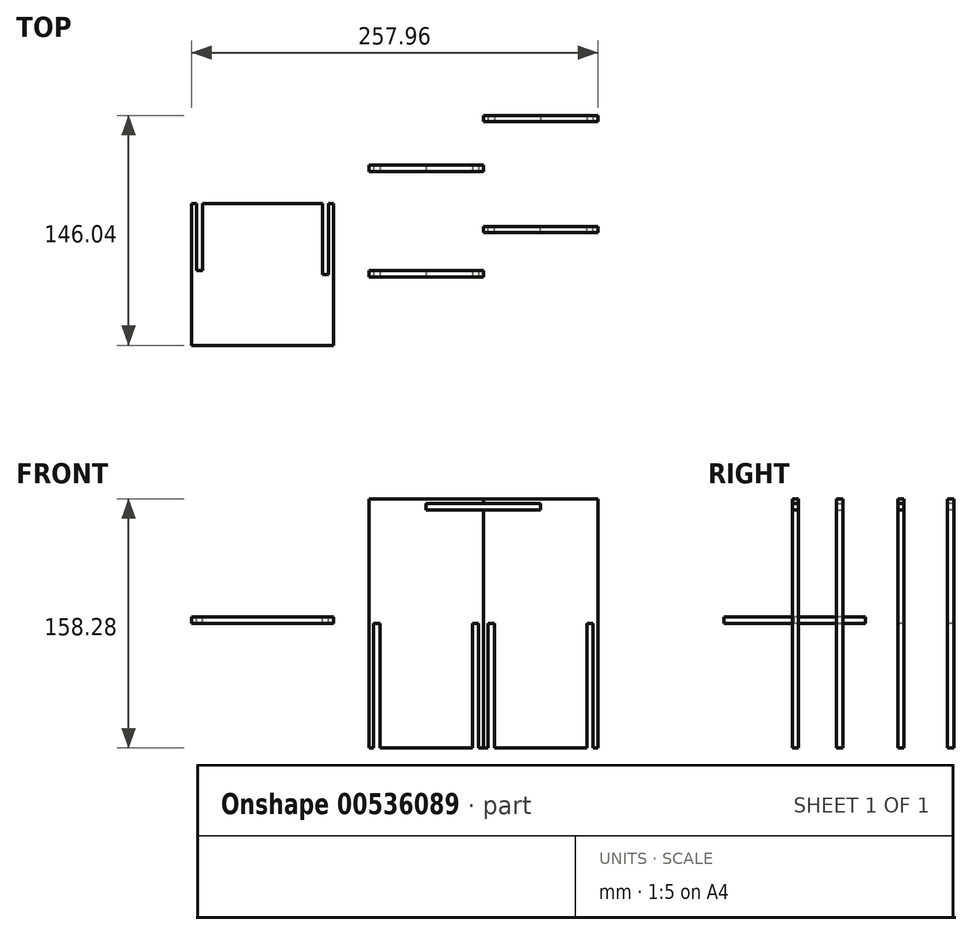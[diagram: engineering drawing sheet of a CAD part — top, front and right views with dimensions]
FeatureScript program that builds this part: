
annotation { "Feature Type Name" : "Feature", "Feature Type Description" : "" }
export const myFeature = defineFeature(function(context is Context, id is Id, definition is map)
    precondition{}
    {
        {
            var Q0;
            Q0=qCreatedBy(makeId("Front.planeOp"),FACE);
            var sketch = newSketch(context, id + "F0", { "sketchPlane" : qUnion([Q0])});
            skLineSegment(sketch, "E0.bottom", {"start": v(36.36, -79.14) * mm, "end": v(-36.36, -79.14) * mm});
            skLineSegment(sketch, "E0.top", {"start": v(36.36, 79.14) * mm, "end": v(-36.36, 79.14) * mm});
            skLineSegment(sketch, "E0.left", {"start": v(36.36, -79.14) * mm, "end": v(36.36, 79.14) * mm});
            skLineSegment(sketch, "E0.right", {"start": v(-36.36, -79.14) * mm, "end": v(-36.36, 79.14) * mm});
            skPoint(sketch, "E0.middle", {"position": v(0, 0) * mm});
            skSolve(sketch);
        }
        {
            var Q0;
            Q0 = qSketchRegion(id + "F0", true);
            extrude(context, id + "F1", {"entities" : qUnion([Q0]), "depth" : 4 * mm, "offsetDistance" : 25 * mm});
        }
        {
            var Q0;
            Q0=makeQuery(id+"F1.opExtrude","CAP_FACE",FACE,{"disambiguationData":[OSD([sQuery(id+"F0.wireOp",EDGE,"E0.bottom"),sQuery(id+"F0.wireOp",EDGE,"E0.top"),sQuery(id+"F0.wireOp",EDGE,"E0.left"),sQuery(id+"F0.wireOp",EDGE,"E0.right")])],"isStart":false});
            var sketch = newSketch(context, id + "F2", { "sketchPlane" : qUnion([Q0])});
            skLineSegment(sketch, "E1.bottom", {"start": v(-33.36, -79.14) * mm, "end": v(-29.36, -79.14) * mm});
            skLineSegment(sketch, "E1.top", {"start": v(-33.36, 0) * mm, "end": v(-29.36, 0) * mm});
            skLineSegment(sketch, "E1.left", {"start": v(-33.36, -79.14) * mm, "end": v(-33.36, 0) * mm});
            skLineSegment(sketch, "E1.right", {"start": v(-29.36, -79.14) * mm, "end": v(-29.36, 0) * mm});
            skSolve(sketch);
        }
        {
            var Q0;
            Q0 = qSketchRegion(id + "F2", true);
            extrude(context, id + "F3", {"entities" : qUnion([Q0]), "operationType" : NewBodyOperationType.REMOVE, "oppositeDirection" : true, "depth" : 25 * mm, "offsetDistance" : 25 * mm});
        }
        {
            var Q0;
            Q0=makeQuery(id+"F1.opExtrude","CAP_FACE",FACE,{"disambiguationData":[OSD([sQuery(id+"F0.wireOp",EDGE,"E0.bottom"),sQuery(id+"F0.wireOp",EDGE,"E0.top"),sQuery(id+"F0.wireOp",EDGE,"E0.left"),sQuery(id+"F0.wireOp",EDGE,"E0.right")])],"isStart":false});
            var sketch = newSketch(context, id + "F4", { "sketchPlane" : qUnion([Q0])});
            skLineSegment(sketch, "E2.bottom", {"start": v(29.36, -79.14) * mm, "end": v(33.36, -79.14) * mm});
            skLineSegment(sketch, "E2.top", {"start": v(29.36, 0) * mm, "end": v(33.36, 0) * mm});
            skLineSegment(sketch, "E2.left", {"start": v(29.36, -79.14) * mm, "end": v(29.36, 0) * mm});
            skLineSegment(sketch, "E2.right", {"start": v(33.36, -79.14) * mm, "end": v(33.36, 0) * mm});
            skSolve(sketch);
        }
        {
            var Q0;
            Q0 = qSketchRegion(id + "F4", true);
            extrude(context, id + "F5", {"entities" : qUnion([Q0]), "operationType" : NewBodyOperationType.REMOVE, "oppositeDirection" : true, "depth" : 25 * mm, "offsetDistance" : 25 * mm});
        }
        {
            var Q0;
            Q0=makeQuery(id+"F1.opExtrude","CAP_FACE",FACE,{"disambiguationData":[OSD([sQuery(id+"F0.wireOp",EDGE,"E0.bottom"),sQuery(id+"F0.wireOp",EDGE,"E0.top"),sQuery(id+"F0.wireOp",EDGE,"E0.left"),sQuery(id+"F0.wireOp",EDGE,"E0.right")])],"isStart":false});
            var sketch = newSketch(context, id + "F6", { "sketchPlane" : qUnion([Q0])});
            skLineSegment(sketch, "E3.bottom", {"start": v(36.36, 76.14) * mm, "end": v(0, 76.14) * mm});
            skLineSegment(sketch, "E3.top", {"start": v(36.36, 72.14) * mm, "end": v(0, 72.14) * mm});
            skLineSegment(sketch, "E3.left", {"start": v(36.36, 76.14) * mm, "end": v(36.36, 72.14) * mm});
            skLineSegment(sketch, "E3.right", {"start": v(0, 76.14) * mm, "end": v(0, 72.14) * mm});
            skSolve(sketch);
        }
        {
            var Q0;
            Q0 = qSketchRegion(id + "F6", true);
            extrude(context, id + "F7", {"entities" : qUnion([Q0]), "operationType" : NewBodyOperationType.REMOVE, "oppositeDirection" : true, "depth" : 25 * mm, "offsetDistance" : 25 * mm});
        }
        {
            var Q0;
            Q0=makeQuery(id+"F1.opExtrude","CAP_FACE",FACE,{"disambiguationData":[OSD([sQuery(id+"F0.wireOp",EDGE,"E0.bottom"),sQuery(id+"F0.wireOp",EDGE,"E0.top"),sQuery(id+"F0.wireOp",EDGE,"E0.left"),sQuery(id+"F0.wireOp",EDGE,"E0.right")])],"isStart":false});
            var sketch = newSketch(context, id + "F8", { "sketchPlane" : qUnion([Q0])});
            skSolve(sketch);
        }
        {
            var Q0;
            Q0 = qSketchRegion(id + "F8", true);
            var Q1;
            {var subQ4=sQuery(id+"F0.wireOp",EDGE,"E0.top");Q1=makeQuery(id+"F8.imprint","IMPRINT",FACE,{"disambiguationData":[TD([[makeQuery(id+"F8.imprint","IMPRINT",EDGE,{"derivedFrom":makeQuery(id+"F1.opExtrude","CAP_EDGE",EDGE,{"disambiguationData":[OSD([subQ4])],"isStart":false})}),1.0]])]});}
            extrude(context, id + "F9", {"entities" : qUnion([Q0, Q1]), "depth" : 4 * mm, "offsetDistance" : 25 * mm});
        }
        {
            var Q0;
            Q0=makeQuery(id+"F9.opExtrude","SWEPT_BODY",BODY,{"disambiguationData":[OSD([sQuery(id+"F0.wireOp",EDGE,"E0.bottom"),sQuery(id+"F0.wireOp",EDGE,"E0.top"),sQuery(id+"F0.wireOp",EDGE,"E0.left"),sQuery(id+"F0.wireOp",EDGE,"E0.right"),sQuery(id+"F2.wireOp",EDGE,"E1.top"),sQuery(id+"F2.wireOp",EDGE,"E1.left"),sQuery(id+"F2.wireOp",EDGE,"E1.right"),sQuery(id+"F4.wireOp",EDGE,"E2.top"),sQuery(id+"F4.wireOp",EDGE,"E2.left"),sQuery(id+"F4.wireOp",EDGE,"E2.right"),sQuery(id+"F6.wireOp",EDGE,"E3.bottom"),sQuery(id+"F6.wireOp",EDGE,"E3.top"),sQuery(id+"F6.wireOp",EDGE,"E3.right")])]});
            transform(context, id + "F10", {"entities" : qUnion([Q0]), "transformType" : TransformType.TRANSLATION_3D, "dx" : 0 * mm, "dy" : 98.5 * mm, "dz" : 0 * mm, "makeCopy" : false});
        }
        {
            var Q0;
            Q0=makeQuery(id+"F1.opExtrude","CAP_FACE",FACE,{"disambiguationData":[OSD([sQuery(id+"F0.wireOp",EDGE,"E0.bottom"),sQuery(id+"F0.wireOp",EDGE,"E0.top"),sQuery(id+"F0.wireOp",EDGE,"E0.left"),sQuery(id+"F0.wireOp",EDGE,"E0.right")])],"isStart":true});
            var sketch = newSketch(context, id + "F11", { "sketchPlane" : qUnion([Q0])});
            skSolve(sketch);
        }
        {
            var Q0;
            Q0 = qSketchRegion(id + "F11", true);
            var Q1;
            {var subQ4=sQuery(id+"F0.wireOp",EDGE,"E0.top");Q1=makeQuery(id+"F11.imprint","IMPRINT",FACE,{"disambiguationData":[TD([[makeQuery(id+"F11.imprint","IMPRINT",EDGE,{"derivedFrom":makeQuery(id+"F1.opExtrude","CAP_EDGE",EDGE,{"disambiguationData":[OSD([subQ4])],"isStart":true})}),-1.0]])]});}
            extrude(context, id + "F12", {"entities" : qUnion([Q0, Q1]), "depth" : 4 * mm, "offsetDistance" : 25 * mm});
        }
        {
            var Q0;
            Q0=makeQuery(id+"F12.opExtrude","SWEPT_BODY",BODY,{"disambiguationData":[OSD([sQuery(id+"F0.wireOp",EDGE,"E0.bottom"),sQuery(id+"F0.wireOp",EDGE,"E0.top"),sQuery(id+"F0.wireOp",EDGE,"E0.left"),sQuery(id+"F0.wireOp",EDGE,"E0.right"),sQuery(id+"F2.wireOp",EDGE,"E1.top"),sQuery(id+"F2.wireOp",EDGE,"E1.left"),sQuery(id+"F2.wireOp",EDGE,"E1.right"),sQuery(id+"F4.wireOp",EDGE,"E2.top"),sQuery(id+"F4.wireOp",EDGE,"E2.left"),sQuery(id+"F4.wireOp",EDGE,"E2.right"),sQuery(id+"F6.wireOp",EDGE,"E3.bottom"),sQuery(id+"F6.wireOp",EDGE,"E3.top"),sQuery(id+"F6.wireOp",EDGE,"E3.right")])]});
            transform(context, id + "F13", {"entities" : qUnion([Q0]), "transformType" : TransformType.TRANSLATION_3D, "dx" : 0 * mm, "dy" : 63 * mm, "dz" : 0 * mm, "makeCopy" : false});
        }
        {
            var Q0;
            Q0=makeQuery(id+"F1.opExtrude","CAP_FACE",FACE,{"disambiguationData":[OSD([sQuery(id+"F0.wireOp",EDGE,"E0.bottom"),sQuery(id+"F0.wireOp",EDGE,"E0.top"),sQuery(id+"F0.wireOp",EDGE,"E0.left"),sQuery(id+"F0.wireOp",EDGE,"E0.right")])],"isStart":true});
            var sketch = newSketch(context, id + "F14", { "sketchPlane" : qUnion([Q0])});
            skSolve(sketch);
        }
        {
            var Q0;
            Q0 = qSketchRegion(id + "F14", true);
            var Q1;
            {var subQ4=sQuery(id+"F0.wireOp",EDGE,"E0.top");Q1=makeQuery(id+"F14.imprint","IMPRINT",FACE,{"disambiguationData":[TD([[makeQuery(id+"F14.imprint","IMPRINT",EDGE,{"derivedFrom":makeQuery(id+"F1.opExtrude","CAP_EDGE",EDGE,{"disambiguationData":[OSD([subQ4])],"isStart":true})}),-1.0]])]});}
            extrude(context, id + "F15", {"entities" : qUnion([Q0, Q1]), "depth" : 4 * mm, "offsetDistance" : 25 * mm});
        }
        {
            var Q0;
            Q0=makeQuery(id+"F15.opExtrude","SWEPT_BODY",BODY,{"disambiguationData":[OSD([sQuery(id+"F0.wireOp",EDGE,"E0.bottom"),sQuery(id+"F0.wireOp",EDGE,"E0.top"),sQuery(id+"F0.wireOp",EDGE,"E0.left"),sQuery(id+"F0.wireOp",EDGE,"E0.right"),sQuery(id+"F2.wireOp",EDGE,"E1.top"),sQuery(id+"F2.wireOp",EDGE,"E1.left"),sQuery(id+"F2.wireOp",EDGE,"E1.right"),sQuery(id+"F4.wireOp",EDGE,"E2.top"),sQuery(id+"F4.wireOp",EDGE,"E2.left"),sQuery(id+"F4.wireOp",EDGE,"E2.right"),sQuery(id+"F6.wireOp",EDGE,"E3.bottom"),sQuery(id+"F6.wireOp",EDGE,"E3.top"),sQuery(id+"F6.wireOp",EDGE,"E3.right")])]});
            transform(context, id + "F16", {"entities" : qUnion([Q0]), "transformType" : TransformType.TRANSLATION_3D, "dx" : 0 * mm, "dy" : 28 * mm, "dz" : 0 * mm, "makeCopy" : false});
        }
        {
            var Q0;
            Q0=makeQuery(id+"F15.opExtrude","SWEPT_BODY",BODY,{"disambiguationData":[OSD([sQuery(id+"F0.wireOp",EDGE,"E0.bottom"),sQuery(id+"F0.wireOp",EDGE,"E0.top"),sQuery(id+"F0.wireOp",EDGE,"E0.left"),sQuery(id+"F0.wireOp",EDGE,"E0.right"),sQuery(id+"F2.wireOp",EDGE,"E1.top"),sQuery(id+"F2.wireOp",EDGE,"E1.left"),sQuery(id+"F2.wireOp",EDGE,"E1.right"),sQuery(id+"F4.wireOp",EDGE,"E2.top"),sQuery(id+"F4.wireOp",EDGE,"E2.left"),sQuery(id+"F4.wireOp",EDGE,"E2.right"),sQuery(id+"F6.wireOp",EDGE,"E3.bottom"),sQuery(id+"F6.wireOp",EDGE,"E3.top"),sQuery(id+"F6.wireOp",EDGE,"E3.right")])]});
            var Q1;
            {var subQ0=sQuery(id+"F0.wireOp",EDGE,"E0.bottom");var subQ1=sQuery(id+"F0.wireOp",EDGE,"E0.left");Q1=makeQuery(id+"F15.opExtrude","CAP_EDGE",EDGE,{"disambiguationData":[OSD([subQ1]),TDD([makeQuery(id+"F14.imprint","IMPRINT",EDGE,{"derivedFrom":makeQuery(id+"F7.boolean.opBoolean","SPLIT",EDGE,{"disambiguationData":[TD([makeQuery(id+"F1.opExtrude","SWEPT_FACE",FACE,{"disambiguationData":[OSD([subQ0])]})])],"derivedFrom":makeQuery(id+"F1.opExtrude","CAP_EDGE",EDGE,{"disambiguationData":[OSD([subQ1])],"isStart":true})})})])],"isStart":true});}
            transform(context, id + "F17", {"entities" : qUnion([Q0]), "transformType" : TransformType.ROTATION, "transformAxis" : qUnion([Q1]), "angle" : 180 * degree, "oppositeDirection" : true, "makeCopy" : false});
        }
        {
            var Q0;
            Q0=makeQuery(id+"F9.opExtrude","SWEPT_BODY",BODY,{"disambiguationData":[OSD([sQuery(id+"F0.wireOp",EDGE,"E0.bottom"),sQuery(id+"F0.wireOp",EDGE,"E0.top"),sQuery(id+"F0.wireOp",EDGE,"E0.left"),sQuery(id+"F0.wireOp",EDGE,"E0.right"),sQuery(id+"F2.wireOp",EDGE,"E1.top"),sQuery(id+"F2.wireOp",EDGE,"E1.left"),sQuery(id+"F2.wireOp",EDGE,"E1.right"),sQuery(id+"F4.wireOp",EDGE,"E2.top"),sQuery(id+"F4.wireOp",EDGE,"E2.left"),sQuery(id+"F4.wireOp",EDGE,"E2.right"),sQuery(id+"F6.wireOp",EDGE,"E3.bottom"),sQuery(id+"F6.wireOp",EDGE,"E3.top"),sQuery(id+"F6.wireOp",EDGE,"E3.right")])]});
            var Q1;
            {var subQ0=sQuery(id+"F0.wireOp",EDGE,"E0.bottom");var subQ1=sQuery(id+"F0.wireOp",EDGE,"E0.left");Q1=makeQuery(id+"F9.opExtrude","CAP_EDGE",EDGE,{"disambiguationData":[OSD([subQ1]),TDD([makeQuery(id+"F8.imprint","IMPRINT",EDGE,{"derivedFrom":makeQuery(id+"F7.boolean.opBoolean","SPLIT",EDGE,{"disambiguationData":[TD([makeQuery(id+"F1.opExtrude","SWEPT_FACE",FACE,{"disambiguationData":[OSD([subQ0])]})])],"derivedFrom":makeQuery(id+"F1.opExtrude","CAP_EDGE",EDGE,{"disambiguationData":[OSD([subQ1])],"isStart":false})})})])],"isStart":true});}
            transform(context, id + "F18", {"entities" : qUnion([Q0]), "transformType" : TransformType.ROTATION, "transformAxis" : qUnion([Q1]), "angle" : 180 * degree, "makeCopy" : false});
        }
        {
            var Q0;
            Q0=qCreatedBy(makeId("Top.planeOp"),FACE);
            var sketch = newSketch(context, id + "F19", { "sketchPlane" : qUnion([Q0])});
            skLineSegment(sketch, "E4.bottom", {"start": v(-148.88, 42.46) * mm, "end": v(-58.88, 42.46) * mm});
            skLineSegment(sketch, "E4.top", {"start": v(-148.88, -47.54) * mm, "end": v(-58.88, -47.54) * mm});
            skLineSegment(sketch, "E4.left", {"start": v(-148.88, 42.46) * mm, "end": v(-148.88, -47.54) * mm});
            skLineSegment(sketch, "E4.right", {"start": v(-58.88, 42.46) * mm, "end": v(-58.88, -47.54) * mm});
            skSolve(sketch);
        }
        {
            var Q0;
            Q0=makeQuery(id+"F19.imprint","IMPRINT",FACE,{"disambiguationData":[TD([[makeQuery(id+"F19.imprint","IMPRINT",EDGE,{"derivedFrom":sQuery(id+"F19.wireOp",EDGE,"E4.bottom")}),-1.0]])]});
            extrude(context, id + "F20", {"entities" : qUnion([Q0]), "depth" : 4 * mm, "offsetDistance" : 25 * mm});
        }
        {
            var Q0;
            Q0=makeQuery(id+"F20.opExtrude","CAP_FACE",FACE,{"disambiguationData":[OSD([sQuery(id+"F19.wireOp",EDGE,"E4.bottom"),sQuery(id+"F19.wireOp",EDGE,"E4.top"),sQuery(id+"F19.wireOp",EDGE,"E4.left"),sQuery(id+"F19.wireOp",EDGE,"E4.right")])],"isStart":false});
            var sketch = newSketch(context, id + "F21", { "sketchPlane" : qUnion([Q0])});
            skLineSegment(sketch, "E5", {"start": v(-148.88, -2.54) * mm, "end": v(-58.88, -2.54) * mm});
            skLineSegment(sketch, "E6.bottom", {"start": v(-65.88, 42.46) * mm, "end": v(-61.88, 42.46) * mm});
            skLineSegment(sketch, "E6.top", {"start": v(-65.88, -2.54) * mm, "end": v(-61.88, -2.54) * mm});
            skLineSegment(sketch, "E6.left", {"start": v(-65.88, 42.46) * mm, "end": v(-65.88, -2.54) * mm});
            skLineSegment(sketch, "E6.right", {"start": v(-61.88, 42.46) * mm, "end": v(-61.88, -2.54) * mm});
            skSolve(sketch);
        }
        {
            var Q0;
            Q0 = qSketchRegion(id + "F21", true);
            extrude(context, id + "F22", {"entities" : qUnion([Q0]), "operationType" : NewBodyOperationType.REMOVE, "oppositeDirection" : true, "depth" : 25 * mm, "offsetDistance" : 25 * mm});
        }
        {
            var Q0;
            Q0=makeQuery(id+"F20.opExtrude","CAP_FACE",FACE,{"disambiguationData":[OSD([sQuery(id+"F19.wireOp",EDGE,"E4.bottom"),sQuery(id+"F19.wireOp",EDGE,"E4.top"),sQuery(id+"F19.wireOp",EDGE,"E4.left"),sQuery(id+"F19.wireOp",EDGE,"E4.right")])],"isStart":false});
            var sketch = newSketch(context, id + "F23", { "sketchPlane" : qUnion([Q0])});
            skLineSegment(sketch, "E7.bottom", {"start": v(-145.88, 42.46) * mm, "end": v(-141.88, 42.46) * mm});
            skLineSegment(sketch, "E7.top", {"start": v(-145.88, 0) * mm, "end": v(-141.88, 0) * mm});
            skLineSegment(sketch, "E7.left", {"start": v(-145.88, 42.46) * mm, "end": v(-145.88, 0) * mm});
            skLineSegment(sketch, "E7.right", {"start": v(-141.88, 42.46) * mm, "end": v(-141.88, 0) * mm});
            skSolve(sketch);
        }
        {
            var Q0;
            Q0 = qSketchRegion(id + "F23", true);
            extrude(context, id + "F24", {"entities" : qUnion([Q0]), "operationType" : NewBodyOperationType.REMOVE, "oppositeDirection" : true, "depth" : 25 * mm, "offsetDistance" : 25 * mm});
        }
    });
